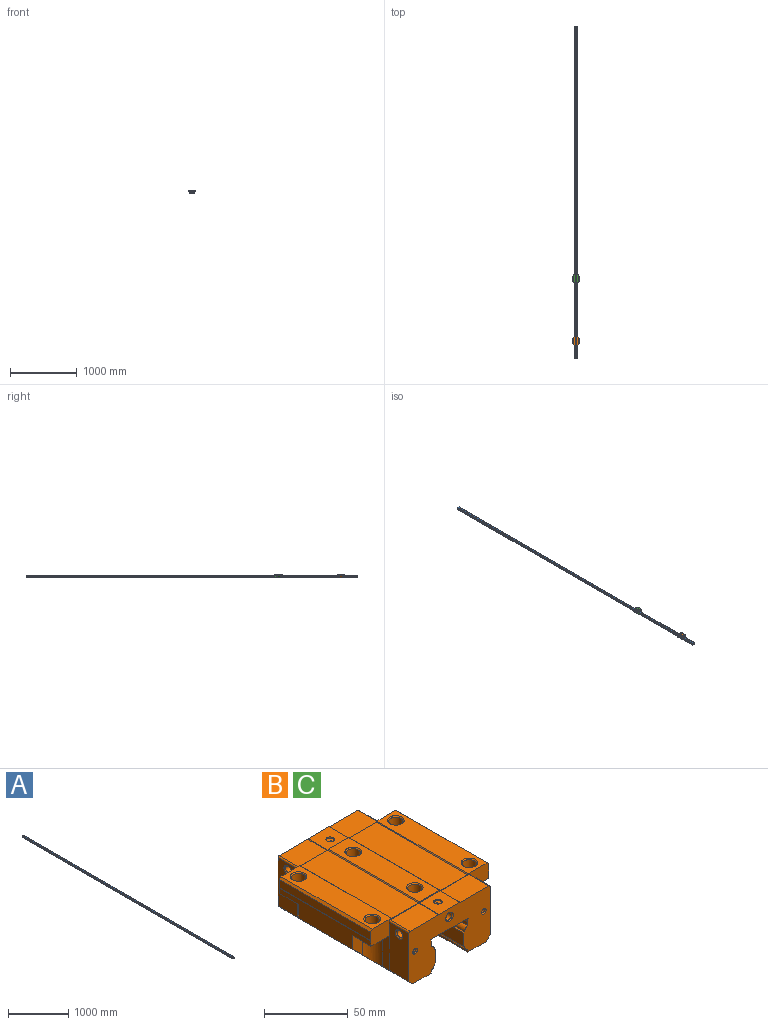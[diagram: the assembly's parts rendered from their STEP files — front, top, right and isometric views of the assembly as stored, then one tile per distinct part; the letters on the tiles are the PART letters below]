
ASSEMBLY  parts=3 mates=4
PART A: 240 faces, bbox 34x4956.5x31.9 mm
  f0: cylinder r=4.5mm len=18.05mm, axis (0,0,1), area 510.3mm2, adj f1,f184
  f1: plane 15x15mm, normal (0,0,1), area 113.1mm2, adj f0,f2
  f2: cylinder r=7.5mm len=15mm, axis (0,0,1), area 636.2mm2, adj f1,f210
  f3: cylinder r=4.5mm len=18.05mm, axis (0,0,1), area 510.3mm2, adj f4,f184
  f4: plane 15x15mm, normal (0,0,1), area 113.1mm2, adj f3,f5
  f5: cylinder r=7.5mm len=15mm, axis (0,0,1), area 636.2mm2, adj f4,f210
  f6: cylinder r=4.5mm len=18.05mm, axis (0,0,1), area 510.3mm2, adj f7,f184
  f7: plane 15x15mm, normal (0,0,1), area 113.1mm2, adj f6,f8
  f8: cylinder r=7.5mm len=15mm, axis (0,0,1), area 636.2mm2, adj f7,f210
  f9: cylinder r=4.5mm len=18.05mm, axis (0,0,1), area 510.3mm2, adj f10,f184
  f10: plane 15x15mm, normal (0,0,1), area 113.1mm2, adj f9,f11
  f11: cylinder r=7.5mm len=15mm, axis (0,0,1), area 636.2mm2, adj f10,f210
  f12: cylinder r=4.5mm len=18.05mm, axis (0,0,1), area 510.3mm2, adj f13,f184
  f13: plane 15x15mm, normal (0,0,1), area 113.1mm2, adj f12,f14
  f14: cylinder r=7.5mm len=15mm, axis (0,0,1), area 636.2mm2, adj f13,f210
  f15: cylinder r=4.5mm len=18.05mm, axis (0,0,1), area 510.3mm2, adj f16,f184
  f16: plane 15x15mm, normal (0,0,1), area 113.1mm2, adj f15,f17
  f17: cylinder r=7.5mm len=15mm, axis (0,0,1), area 636.2mm2, adj f16,f210
  f18: cylinder r=4.5mm len=18.05mm, axis (0,0,1), area 510.3mm2, adj f19,f184
  f19: plane 15x15mm, normal (0,0,1), area 113.1mm2, adj f18,f20
  f20: cylinder r=7.5mm len=15mm, axis (0,0,1), area 636.2mm2, adj f19,f210
  f21: cylinder r=4.5mm len=18.05mm, axis (0,0,1), area 510.3mm2, adj f22,f184
  f22: plane 15x15mm, normal (0,0,1), area 113.1mm2, adj f21,f23
  f23: cylinder r=7.5mm len=15mm, axis (0,0,1), area 636.2mm2, adj f22,f210
  f24: cylinder r=4.5mm len=18.05mm, axis (0,0,1), area 510.3mm2, adj f25,f184
  f25: plane 15x15mm, normal (0,0,1), area 113.1mm2, adj f24,f26
  f26: cylinder r=7.5mm len=15mm, axis (0,0,1), area 636.2mm2, adj f25,f210
  f27: cylinder r=4.5mm len=18.05mm, axis (0,0,1), area 510.3mm2, adj f28,f184
  f28: plane 15x15mm, normal (0,0,1), area 113.1mm2, adj f27,f29
  f29: cylinder r=7.5mm len=15mm, axis (0,0,1), area 636.2mm2, adj f28,f210
  f30: cylinder r=4.5mm len=18.05mm, axis (0,0,1), area 510.3mm2, adj f31,f184
  f31: plane 15x15mm, normal (0,0,1), area 113.1mm2, adj f30,f32
  f32: cylinder r=7.5mm len=15mm, axis (0,0,1), area 636.2mm2, adj f31,f210
  f33: cylinder r=4.5mm len=18.05mm, axis (0,0,1), area 510.3mm2, adj f34,f184
  f34: plane 15x15mm, normal (0,0,1), area 113.1mm2, adj f33,f35
  f35: cylinder r=7.5mm len=15mm, axis (0,0,1), area 636.2mm2, adj f34,f210
  f36: cylinder r=4.5mm len=18.05mm, axis (0,0,1), area 510.3mm2, adj f37,f184
  f37: plane 15x15mm, normal (0,0,1), area 113.1mm2, adj f36,f38
  f38: cylinder r=7.5mm len=15mm, axis (0,0,1), area 636.2mm2, adj f37,f210
  f39: cylinder r=4.5mm len=18.05mm, axis (0,0,1), area 510.3mm2, adj f40,f184
  f40: plane 15x15mm, normal (0,0,1), area 113.1mm2, adj f39,f41
  f41: cylinder r=7.5mm len=15mm, axis (0,0,1), area 636.2mm2, adj f40,f210
  f42: cylinder r=4.5mm len=18.05mm, axis (0,0,1), area 510.3mm2, adj f43,f184
  f43: plane 15x15mm, normal (0,0,1), area 113.1mm2, adj f42,f44
  f44: cylinder r=7.5mm len=15mm, axis (0,0,1), area 636.2mm2, adj f43,f210
  f45: cylinder r=4.5mm len=18.05mm, axis (0,0,1), area 510.3mm2, adj f46,f184
  f46: plane 15x15mm, normal (0,0,1), area 113.1mm2, adj f45,f47
  f47: cylinder r=7.5mm len=15mm, axis (0,0,1), area 636.2mm2, adj f46,f210
  f48: cylinder r=4.5mm len=18.05mm, axis (0,0,1), area 510.3mm2, adj f49,f184
  f49: plane 15x15mm, normal (0,0,1), area 113.1mm2, adj f48,f50
  f50: cylinder r=7.5mm len=15mm, axis (0,0,1), area 636.2mm2, adj f49,f210
  f51: cylinder r=4.5mm len=18.05mm, axis (0,0,1), area 510.3mm2, adj f52,f184
  f52: plane 15x15mm, normal (0,0,1), area 113.1mm2, adj f51,f53
  f53: cylinder r=7.5mm len=15mm, axis (0,0,1), area 636.2mm2, adj f52,f210
  f54: cylinder r=4.5mm len=18.05mm, axis (0,0,1), area 510.3mm2, adj f55,f184
  f55: plane 15x15mm, normal (0,0,1), area 113.1mm2, adj f54,f56
  f56: cylinder r=7.5mm len=15mm, axis (0,0,1), area 636.2mm2, adj f55,f210
  f57: cylinder r=4.5mm len=18.05mm, axis (0,0,1), area 510.3mm2, adj f58,f184
  f58: plane 15x15mm, normal (0,0,1), area 113.1mm2, adj f57,f59
  f59: cylinder r=7.5mm len=15mm, axis (0,0,1), area 636.2mm2, adj f58,f210
  f60: cylinder r=4.5mm len=18.05mm, axis (0,0,1), area 510.3mm2, adj f61,f184
  f61: plane 15x15mm, normal (0,0,1), area 113.1mm2, adj f60,f62
  f62: cylinder r=7.5mm len=15mm, axis (0,0,1), area 636.2mm2, adj f61,f210
  f63: cylinder r=4.5mm len=18.05mm, axis (0,0,1), area 510.3mm2, adj f64,f184
  f64: plane 15x15mm, normal (0,0,1), area 113.1mm2, adj f63,f65
  f65: cylinder r=7.5mm len=15mm, axis (0,0,1), area 636.2mm2, adj f64,f210
  f66: cylinder r=4.5mm len=18.05mm, axis (0,0,1), area 510.3mm2, adj f67,f184
  f67: plane 15x15mm, normal (0,0,1), area 113.1mm2, adj f66,f68
  f68: cylinder r=7.5mm len=15mm, axis (0,0,1), area 636.2mm2, adj f67,f210
  f69: cylinder r=4.5mm len=18.05mm, axis (0,0,1), area 510.3mm2, adj f70,f184
  f70: plane 15x15mm, normal (0,0,1), area 113.1mm2, adj f69,f71
  f71: cylinder r=7.5mm len=15mm, axis (0,0,1), area 636.2mm2, adj f70,f210
  f72: cylinder r=4.5mm len=18.05mm, axis (0,0,1), area 510.3mm2, adj f73,f184
  f73: plane 15x15mm, normal (0,0,1), area 113.1mm2, adj f72,f74
  f74: cylinder r=7.5mm len=15mm, axis (0,0,1), area 636.2mm2, adj f73,f210
  f75: cylinder r=4.5mm len=18.05mm, axis (0,0,1), area 510.3mm2, adj f76,f184
  f76: plane 15x15mm, normal (0,0,1), area 113.1mm2, adj f75,f77
  f77: cylinder r=7.5mm len=15mm, axis (0,0,1), area 636.2mm2, adj f76,f210
  f78: cylinder r=4.5mm len=18.05mm, axis (0,0,1), area 510.3mm2, adj f79,f184
  f79: plane 15x15mm, normal (0,0,1), area 113.1mm2, adj f78,f80
  f80: cylinder r=7.5mm len=15mm, axis (0,0,1), area 636.2mm2, adj f79,f210
  f81: cylinder r=4.5mm len=18.05mm, axis (0,0,1), area 510.3mm2, adj f82,f184
  f82: plane 15x15mm, normal (0,0,1), area 113.1mm2, adj f81,f83
  f83: cylinder r=7.5mm len=15mm, axis (0,0,1), area 636.2mm2, adj f82,f210
  f84: cylinder r=4.5mm len=18.05mm, axis (0,0,1), area 510.3mm2, adj f85,f184
  f85: plane 15x15mm, normal (0,0,1), area 113.1mm2, adj f84,f86
  f86: cylinder r=7.5mm len=15mm, axis (0,0,1), area 636.2mm2, adj f85,f210
  f87: cylinder r=4.5mm len=18.05mm, axis (0,0,1), area 510.3mm2, adj f88,f184
  f88: plane 15x15mm, normal (0,0,1), area 113.1mm2, adj f87,f89
  f89: cylinder r=7.5mm len=15mm, axis (0,0,1), area 636.2mm2, adj f88,f210
  f90: cylinder r=4.5mm len=18.05mm, axis (0,0,1), area 510.3mm2, adj f91,f184
  f91: plane 15x15mm, normal (0,0,1), area 113.1mm2, adj f90,f92
  f92: cylinder r=7.5mm len=15mm, axis (0,0,1), area 636.2mm2, adj f91,f210
  f93: cylinder r=4.5mm len=18.05mm, axis (0,0,1), area 510.3mm2, adj f94,f184
  f94: plane 15x15mm, normal (0,0,1), area 113.1mm2, adj f93,f95
  f95: cylinder r=7.5mm len=15mm, axis (0,0,1), area 636.2mm2, adj f94,f210
  f96: cylinder r=4.5mm len=18.05mm, axis (0,0,1), area 510.3mm2, adj f97,f184
  f97: plane 15x15mm, normal (0,0,1), area 113.1mm2, adj f96,f98
  f98: cylinder r=7.5mm len=15mm, axis (0,0,1), area 636.2mm2, adj f97,f210
  f99: cylinder r=4.5mm len=18.05mm, axis (0,0,1), area 510.3mm2, adj f100,f184
  f100: plane 15x15mm, normal (0,0,1), area 113.1mm2, adj f99,f101
  f101: cylinder r=7.5mm len=15mm, axis (0,0,1), area 636.2mm2, adj f100,f210
  f102: cylinder r=4.5mm len=18.05mm, axis (0,0,1), area 510.3mm2, adj f103,f184
  f103: plane 15x15mm, normal (0,0,1), area 113.1mm2, adj f102,f104
  f104: cylinder r=7.5mm len=15mm, axis (0,0,1), area 636.2mm2, adj f103,f210
  f105: cylinder r=4.5mm len=18.05mm, axis (0,0,1), area 510.3mm2, adj f106,f184
  f106: plane 15x15mm, normal (0,0,1), area 113.1mm2, adj f105,f107
  f107: cylinder r=7.5mm len=15mm, axis (0,0,1), area 636.2mm2, adj f106,f210
  f108: cylinder r=4.5mm len=18.05mm, axis (0,0,1), area 510.3mm2, adj f109,f184
  f109: plane 15x15mm, normal (0,0,1), area 113.1mm2, adj f108,f110
  f110: cylinder r=7.5mm len=15mm, axis (0,0,1), area 636.2mm2, adj f109,f210
  f111: cylinder r=4.5mm len=18.05mm, axis (0,0,1), area 510.3mm2, adj f112,f184
  f112: plane 15x15mm, normal (0,0,1), area 113.1mm2, adj f111,f113
  f113: cylinder r=7.5mm len=15mm, axis (0,0,1), area 636.2mm2, adj f112,f210
  f114: cylinder r=4.5mm len=18.05mm, axis (0,0,1), area 510.3mm2, adj f115,f184
  f115: plane 15x15mm, normal (0,0,1), area 113.1mm2, adj f114,f116
  f116: cylinder r=7.5mm len=15mm, axis (0,0,1), area 636.2mm2, adj f115,f210
  f117: cylinder r=4.5mm len=18.05mm, axis (0,0,1), area 510.3mm2, adj f118,f184
  f118: plane 15x15mm, normal (0,0,1), area 113.1mm2, adj f117,f119
  f119: cylinder r=7.5mm len=15mm, axis (0,0,1), area 636.2mm2, adj f118,f210
  f120: cylinder r=4.5mm len=18.05mm, axis (0,0,1), area 510.3mm2, adj f121,f184
  f121: plane 15x15mm, normal (0,0,1), area 113.1mm2, adj f120,f122
  f122: cylinder r=7.5mm len=15mm, axis (0,0,1), area 636.2mm2, adj f121,f210
  f123: cylinder r=4.5mm len=18.05mm, axis (0,0,1), area 510.3mm2, adj f124,f184
  f124: plane 15x15mm, normal (0,0,1), area 113.1mm2, adj f123,f125
  f125: cylinder r=7.5mm len=15mm, axis (0,0,1), area 636.2mm2, adj f124,f210
  f126: cylinder r=4.5mm len=18.05mm, axis (0,0,1), area 510.3mm2, adj f127,f184
  f127: plane 15x15mm, normal (0,0,1), area 113.1mm2, adj f126,f128
  f128: cylinder r=7.5mm len=15mm, axis (0,0,1), area 636.2mm2, adj f127,f210
  f129: cylinder r=4.5mm len=18.05mm, axis (0,0,1), area 510.3mm2, adj f130,f184
  f130: plane 15x15mm, normal (0,0,1), area 113.1mm2, adj f129,f131
  f131: cylinder r=7.5mm len=15mm, axis (0,0,1), area 636.2mm2, adj f130,f210
  f132: cylinder r=4.5mm len=18.05mm, axis (0,0,1), area 510.3mm2, adj f133,f184
  f133: plane 15x15mm, normal (0,0,1), area 113.1mm2, adj f132,f134
  f134: cylinder r=7.5mm len=15mm, axis (0,0,1), area 636.2mm2, adj f133,f210
  f135: cylinder r=4.5mm len=18.05mm, axis (0,0,1), area 510.3mm2, adj f136,f184
  f136: plane 15x15mm, normal (0,0,1), area 113.1mm2, adj f135,f137
  f137: cylinder r=7.5mm len=15mm, axis (0,0,1), area 636.2mm2, adj f136,f210
  f138: cylinder r=4.5mm len=18.05mm, axis (0,0,1), area 510.3mm2, adj f139,f184
  f139: plane 15x15mm, normal (0,0,1), area 113.1mm2, adj f138,f140
  f140: cylinder r=7.5mm len=15mm, axis (0,0,1), area 636.2mm2, adj f139,f210
  f141: cylinder r=4.5mm len=18.05mm, axis (0,0,1), area 510.3mm2, adj f142,f184
  f142: plane 15x15mm, normal (0,0,1), area 113.1mm2, adj f141,f143
  f143: cylinder r=7.5mm len=15mm, axis (0,0,1), area 636.2mm2, adj f142,f210
  f144: cylinder r=4.5mm len=18.05mm, axis (0,0,1), area 510.3mm2, adj f145,f184
  f145: plane 15x15mm, normal (0,0,1), area 113.1mm2, adj f144,f146
  f146: cylinder r=7.5mm len=15mm, axis (0,0,1), area 636.2mm2, adj f145,f210
  f147: cylinder r=4.5mm len=18.05mm, axis (0,0,1), area 510.3mm2, adj f148,f184
  f148: plane 15x15mm, normal (0,0,1), area 113.1mm2, adj f147,f149
  f149: cylinder r=7.5mm len=15mm, axis (0,0,1), area 636.2mm2, adj f148,f210
  f150: cylinder r=4.5mm len=18.05mm, axis (0,0,1), area 510.3mm2, adj f151,f184
  f151: plane 15x15mm, normal (0,0,1), area 113.1mm2, adj f150,f152
  f152: cylinder r=7.5mm len=15mm, axis (0,0,1), area 636.2mm2, adj f151,f210
  f153: cylinder r=4.5mm len=18.05mm, axis (0,0,1), area 510.3mm2, adj f154,f184
  f154: plane 15x15mm, normal (0,0,1), area 113.1mm2, adj f153,f155
  f155: cylinder r=7.5mm len=15mm, axis (0,0,1), area 636.2mm2, adj f154,f210
  f156: cylinder r=4.5mm len=18.05mm, axis (0,0,1), area 510.3mm2, adj f157,f184
  f157: plane 15x15mm, normal (0,0,1), area 113.1mm2, adj f156,f158
  f158: cylinder r=7.5mm len=15mm, axis (0,0,1), area 636.2mm2, adj f157,f210
  f159: cylinder r=4.5mm len=18.05mm, axis (0,0,1), area 510.3mm2, adj f160,f184
  f160: plane 15x15mm, normal (0,0,1), area 113.1mm2, adj f159,f161
  f161: cylinder r=7.5mm len=15mm, axis (0,0,1), area 636.2mm2, adj f160,f210
  f162: cylinder r=4.5mm len=18.05mm, axis (0,0,1), area 510.3mm2, adj f163,f184
  f163: plane 15x15mm, normal (0,0,1), area 113.1mm2, adj f162,f164
  f164: cylinder r=7.5mm len=15mm, axis (0,0,1), area 636.2mm2, adj f163,f210
  f165: cylinder r=4.5mm len=18.05mm, axis (0,0,1), area 510.3mm2, adj f166,f184
  f166: plane 15x15mm, normal (0,0,1), area 113.1mm2, adj f165,f167
  f167: cylinder r=7.5mm len=15mm, axis (0,0,1), area 636.2mm2, adj f166,f210
  f168: cylinder r=4.5mm len=18.05mm, axis (0,0,1), area 510.3mm2, adj f169,f184
  f169: plane 15x15mm, normal (0,0,1), area 113.1mm2, adj f168,f170
  f170: cylinder r=7.5mm len=15mm, axis (0,0,1), area 636.2mm2, adj f169,f210
  f171: cylinder r=4.5mm len=18.05mm, axis (0,0,1), area 510.3mm2, adj f172,f184
  f172: plane 15x15mm, normal (0,0,1), area 113.1mm2, adj f171,f173
  f173: cylinder r=7.5mm len=15mm, axis (0,0,1), area 636.2mm2, adj f172,f210
  f174: cylinder r=4.5mm len=18.05mm, axis (0,0,1), area 510.3mm2, adj f175,f184
  f175: plane 15x15mm, normal (0,0,1), area 113.1mm2, adj f174,f176
  f176: cylinder r=7.5mm len=15mm, axis (0,0,1), area 636.2mm2, adj f175,f210
  f177: cylinder r=4.5mm len=18.05mm, axis (0,0,1), area 510.3mm2, adj f178,f184
  f178: plane 15x15mm, normal (0,0,1), area 113.1mm2, adj f177,f179
  f179: cylinder r=7.5mm len=15mm, axis (0,0,1), area 636.2mm2, adj f178,f210
  f180: plane 4956.54x5.07mm, normal (-1,0,0), area 25140mm2, adj f181,f231,f232,f233
  f181: plane 4956.54x1mm, normal (-0.71,0,-0.71), area 7009.6mm2, adj f180,f182,f232,f233
  f182: plane 4956.54x9.8mm, normal (0,0,-1), area 48574.1mm2, adj f181,f183,f232,f233
  f183: plane 4956.54x0.3mm, normal (0.71,0,-0.71), area 2102.9mm2, adj f182,f184,f232,f233
  f184: plane 4956.54x11.8mm, normal (0,0,-1), area 54543.4mm2, adj f0,f3,f6,f9,f12,f15,f18,f21
  f185: plane 4956.54x0.3mm, normal (-0.71,0,-0.71), area 2102.9mm2, adj f184,f186,f232,f233
  f186: plane 4956.54x9.8mm, normal (0,0,-1), area 48574.1mm2, adj f185,f187,f232,f233
  f187: plane 4956.54x1mm, normal (0.71,0,-0.71), area 7009.6mm2, adj f186,f188,f232,f233
  f188: plane 4956.54x5.07mm, normal (1,0,0), area 25140mm2, adj f187,f189,f232,f233
  f189: cylinder r=0.8mm len=4956.54mm, axis (0,1,0), area 4152.3mm2, adj f188,f190,f232,f233
  f190: plane 4956.54x0.7mm, normal (0.5,0,0.87), area 4006.3mm2, adj f189,f191,f232,f233
  f191: cylinder r=0.8mm len=4956.54mm, axis (0,1,0), area 4152.4mm2, adj f190,f192,f232,f233
  f192: plane 4956.54x1.75mm, normal (1,0,0), area 8650.2mm2, adj f191,f193,f232,f233
  f193: cylinder r=0.3mm len=4956.54mm, axis (0,1,0), area 1979.4mm2, adj f192,f194,f232,f233
  f194: cylinder r=3.24mm len=4956.54mm, axis (0,1,0), area 18238.7mm2, adj f193,f195,f232,f233
  f195: cylinder r=0.3mm len=4956.54mm, axis (0,1,0), area 877.1mm2, adj f194,f196,f232,f233
  f196: plane 4956.54x0.8mm, normal (0.71,0,0.71), area 5574.5mm2, adj f195,f197,f232,f233
  f197: cylinder r=0.8mm len=4956.54mm, axis (0,1,0), area 3114.3mm2, adj f196,f198,f232,f233
  f198: plane 4956.54x9.14mm, normal (1,0,0), area 45289.2mm2, adj f197,f199,f232,f233
  f199: cylinder r=0.8mm len=4956.54mm, axis (0,1,0), area 3114.3mm2, adj f198,f200,f232,f233
  f200: plane 4956.54x0.8mm, normal (0.71,0,-0.71), area 5574.5mm2, adj f199,f201,f232,f233
  f201: cylinder r=0.3mm len=4956.54mm, axis (0,1,0), area 877.1mm2, adj f200,f202,f232,f233
  f202: cylinder r=3.24mm len=4956.54mm, axis (0,1,0), area 18238.7mm2, adj f201,f203,f232,f233
  f203: cylinder r=0.3mm len=4956.54mm, axis (0,1,0), area 1979.4mm2, adj f202,f204,f232,f233
  f204: plane 4956.54x1.96mm, normal (1,0,0), area 9714.9mm2, adj f203,f205,f232,f233
  f205: cylinder r=0.5mm len=4956.54mm, axis (0,1,0), area 1946.3mm2, adj f204,f206,f232,f233
  f206: plane 4956.54x0.3mm, normal (0.71,0,0.71), area 2099mm2, adj f205,f207,f232,f233
  f207: cylinder r=0.5mm len=4956.54mm, axis (0,1,0), area 2595.3mm2, adj f206,f208,f232,f233
  f208: plane 4956.54x0.73mm, normal (0.97,0,-0.26), area 3754.9mm2, adj f207,f209,f232,f233
  f209: cylinder r=0.5mm len=4956.54mm, axis (0,1,0), area 4541.6mm2, adj f208,f210,f232,f233
  f210: plane 4956.54x29.28mm, normal (0,0,1), area 134147.6mm2, adj f2,f5,f8,f11,f14,f17,f20,f23
  f211: cylinder r=0.5mm len=4956.54mm, axis (0,1,0), area 4541.6mm2, adj f210,f212,f232,f233
  f212: plane 4956.54x0.73mm, normal (-0.97,0,-0.26), area 3754.9mm2, adj f211,f213,f232,f233
  f213: cylinder r=0.5mm len=4956.54mm, axis (0,1,0), area 2595.3mm2, adj f212,f214,f232,f233
  f214: plane 4956.54x0.3mm, normal (-0.71,0,0.71), area 2099mm2, adj f213,f215,f232,f233
  f215: cylinder r=0.5mm len=4956.54mm, axis (0,1,0), area 1946.3mm2, adj f214,f216,f232,f233
  f216: plane 4956.54x1.96mm, normal (-1,0,0), area 9714.9mm2, adj f215,f217,f232,f233
  f217: cylinder r=0.3mm len=4956.54mm, axis (0,1,0), area 1979.4mm2, adj f216,f218,f232,f233
  f218: cylinder r=3.24mm len=4956.54mm, axis (0,1,0), area 18238.7mm2, adj f217,f219,f232,f233
  f219: cylinder r=0.3mm len=4956.54mm, axis (0,1,0), area 877.1mm2, adj f218,f220,f232,f233
  f220: plane 4956.54x0.8mm, normal (-0.71,0,-0.71), area 5574.5mm2, adj f219,f221,f232,f233
  f221: cylinder r=0.8mm len=4956.54mm, axis (0,1,0), area 3114.3mm2, adj f220,f222,f232,f233
  f222: plane 4956.54x9.14mm, normal (-1,0,0), area 45289.2mm2, adj f221,f223,f232,f233
  f223: cylinder r=0.8mm len=4956.54mm, axis (0,1,0), area 3114.3mm2, adj f222,f224,f232,f233
  f224: plane 4956.54x0.8mm, normal (-0.71,0,0.71), area 5574.5mm2, adj f223,f225,f232,f233
  f225: cylinder r=0.3mm len=4956.54mm, axis (0,1,0), area 877.1mm2, adj f224,f226,f232,f233
  f226: cylinder r=3.24mm len=4956.54mm, axis (0,1,0), area 18238.7mm2, adj f225,f227,f232,f233
  f227: cylinder r=0.3mm len=4956.54mm, axis (0,1,0), area 1979.4mm2, adj f226,f228,f232,f233
  f228: plane 4956.54x1.75mm, normal (-1,0,0), area 8650.2mm2, adj f227,f229,f232,f233
  f229: cylinder r=0.8mm len=4956.54mm, axis (0,1,0), area 4152.4mm2, adj f228,f230,f232,f233
  f230: plane 4956.54x0.7mm, normal (-0.5,0,0.87), area 4006.3mm2, adj f229,f231,f232,f233
  f231: cylinder r=0.8mm len=4956.54mm, axis (0,1,0), area 4152.3mm2, adj f180,f230,f232,f233
  f232: plane 34x31.85mm, normal (0,-1,0), area 893.9mm2, adj f180,f181,f182,f183,f184,f185,f186,f187
  f233: plane 34x31.85mm, normal (0,1,0), area 893.9mm2, adj f180,f181,f182,f183,f184,f185,f186,f187
  f234: cylinder r=4.5mm len=18.05mm, axis (0,0,1), area 510.3mm2, adj f184,f235
  f235: plane 15x15mm, normal (0,0,1), area 113.1mm2, adj f234,f236
  f236: cylinder r=7.5mm len=15mm, axis (0,0,1), area 636.2mm2, adj f210,f235
  f237: cylinder r=4.5mm len=18.05mm, axis (0,0,1), area 510.3mm2, adj f184,f238
  f238: plane 15x15mm, normal (0,0,1), area 113.1mm2, adj f237,f239
  f239: cylinder r=7.5mm len=15mm, axis (0,0,1), area 636.2mm2, adj f210,f238
PART B: 150 faces, bbox 100x110.5x40.4 mm
  f0: plane 0.8x0.8mm, normal (0,0,1), area 0.5mm2, adj f5
  f1: cone r=1.25mm half-angle=59deg, axis (0,-1,0), area 5.7mm2, adj f8
  f2: cone r=2.5mm half-angle=59deg, axis (0,-1,0), area 22.9mm2, adj f9
  f3: cone r=1.25mm half-angle=59deg, axis (0,-1,0), area 5.7mm2, adj f10
  f4: cone r=2.5mm half-angle=59deg, axis (-1,0,0), area 22.9mm2, adj f11
  f5: cylinder r=0.4mm len=6.5mm, axis (0,0,1), area 16.3mm2, adj f0,f12
  f6: cone r=2.5mm half-angle=59deg, axis (1,0,0), area 22.9mm2, adj f13
  f7: plane 0.8x0.8mm, normal (0,0,1), area 0.5mm2, adj f14
  f8: cylinder r=1.25mm len=5.8mm, axis (0,1,0), area 45.6mm2, adj f1,f21
  f9: cylinder r=2.5mm len=7.3mm, axis (0,1,0), area 114.7mm2, adj f2,f22
  f10: cylinder r=1.25mm len=5.8mm, axis (0,1,0), area 45.6mm2, adj f3,f23
  f11: cylinder r=2.5mm len=7.3mm, axis (1,0,0), area 114.7mm2, adj f4,f24
  f12: plane 5x5mm, normal (0,0,1), area 19.1mm2, adj f5,f26
  f13: cylinder r=2.5mm len=7.3mm, axis (1,0,0), area 114.7mm2, adj f6,f27
  f14: cylinder r=0.4mm len=6.5mm, axis (0,0,1), area 16.3mm2, adj f7,f28
  f15: cone r=2.5mm half-angle=59deg, axis (-1,0,0), area 22.9mm2, adj f38
  f16: cone r=1.25mm half-angle=59deg, axis (0,1,0), area 5.7mm2, adj f40
  f17: cone r=1.25mm half-angle=59deg, axis (0,1,0), area 5.7mm2, adj f41
  f18: cone r=2.5mm half-angle=59deg, axis (0,1,0), area 22.9mm2, adj f42
  f19: plane 17x17mm, normal (0,0,-1), area 170.2mm2, adj f31,f43
  f20: plane 17x17mm, normal (0,0,-1), area 170.2mm2, adj f30,f44
  f21: cone r=1.25mm half-angle=45deg, axis (0,-1,0), area 10mm2, adj f8,f49
  f22: cone r=2.5mm half-angle=45deg, axis (0,-1,0), area 17.7mm2, adj f9,f49
  f23: cone r=1.25mm half-angle=45deg, axis (0,-1,0), area 10mm2, adj f10,f49
  f24: cone r=2.5mm half-angle=45deg, axis (-1,0,0), area 17.7mm2, adj f11,f54
  f25: plane 16.75x3.22mm, normal (-0.71,0,-0.71), area 76.3mm2, adj f34,f45,f47,f49,f54
  f26: cylinder r=2.5mm len=5mm, axis (0,0,1), area 15.7mm2, adj f12,f58
  f27: cone r=2.5mm half-angle=45deg, axis (1,0,0), area 17.7mm2, adj f13,f62
  f28: plane 5x5mm, normal (0,0,1), area 19.1mm2, adj f14,f63
  f29: cylinder r=4.25mm len=10.6mm, axis (0,0,1), area 283.1mm2, adj f52,f64
  f30: cylinder r=4.25mm len=9.5mm, axis (0,0,-1), area 253.7mm2, adj f20,f66
  f31: cylinder r=4.25mm len=9.5mm, axis (0,0,-1), area 253.7mm2, adj f19,f67
  f32: cylinder r=4.25mm len=10.6mm, axis (0,0,1), area 283.1mm2, adj f33,f68
  f33: cone r=4.25mm half-angle=45deg, axis (0,0,-1), area 28.6mm2, adj f32,f70
  f34: plane 26.83x1.7mm, normal (0,1,0), area 44.2mm2, adj f25,f36,f54,f70
  f35: cylinder r=8.5mm len=26.9mm, axis (0,0,1), area 317.9mm2, adj f36,f70,f71,f72
  f36: plane 26.9x7.5mm, normal (-1,0,0), area 201.7mm2, adj f34,f35,f47,f70,f72
  f37: cylinder r=4.25mm len=10.6mm, axis (0,0,1), area 283.1mm2, adj f69,f73
  f38: cylinder r=2.5mm len=7.3mm, axis (1,0,0), area 114.7mm2, adj f15,f77
  f39: cone r=2.5mm half-angle=59deg, axis (1,0,0), area 22.9mm2, adj f79
  f40: cylinder r=1.25mm len=5.8mm, axis (0,1,0), area 45.6mm2, adj f16,f80
  f41: cylinder r=1.25mm len=5.8mm, axis (0,1,0), area 45.6mm2, adj f17,f81
  f42: cylinder r=2.5mm len=7.3mm, axis (0,1,0), area 114.7mm2, adj f18,f82
  f43: cylinder r=8.5mm len=17mm, axis (0,0,-1), area 288.4mm2, adj f19,f91
  f44: cylinder r=8.5mm len=17mm, axis (0,0,-1), area 288.4mm2, adj f20,f91
  f45: plane 16.75x15.48mm, normal (0,0,-1), area 259.3mm2, adj f25,f47,f49,f100
  f46: plane 77x15.5mm, normal (0,0,-1), area 1193.5mm2, adj f47,f48,f72,f100
  f47: plane 17x1.57mm, normal (0,-1,0), area 0.9mm2, adj f25,f36,f45,f46,f72,f100
  f48: plane 17x1.57mm, normal (0,1,0), area 0.9mm2, adj f46,f72,f74,f100,f101,f102
  f49: plane 68.4x39.75mm, normal (0,-1,0), area 1979.4mm2, adj f21,f22,f23,f25,f45,f50,f51,f54
  f50: plane 16.75x3.22mm, normal (0.71,0,-0.71), area 76.3mm2, adj f49,f51,f53,f62,f105
  f51: plane 16.75x15.48mm, normal (0,0,-1), area 259.3mm2, adj f49,f50,f103,f105
  f52: cone r=4.95mm half-angle=45deg, axis (0,0,-1), area 28.6mm2, adj f29,f110
  f53: plane 26.83x1.7mm, normal (0,1,0), area 44.2mm2, adj f50,f62,f106,f110
  f54: plane 35.28x16.75mm, normal (-1,0,0), area 558.8mm2, adj f24,f25,f34,f49,f55,f111
  f55: cylinder r=1mm len=16.75mm, axis (0,-1,0), area 26.3mm2, adj f49,f54,f56,f111
  f56: plane 24.15x16.75mm, normal (0,0,1), area 404.5mm2, adj f49,f55,f57,f111
  f57: plane 16.75x0.25mm, normal (-0.71,0,0.71), area 5.9mm2, adj f49,f56,f58,f111
  f58: plane 17.6x16.75mm, normal (0,0,1), area 275.2mm2, adj f26,f49,f57,f59,f111
  f59: plane 16.75x0.25mm, normal (0.71,0,0.71), area 5.9mm2, adj f49,f58,f60,f111
  f60: plane 24.15x16.75mm, normal (0,0,1), area 404.5mm2, adj f49,f59,f61,f111
  f61: cylinder r=1mm len=16.75mm, axis (0,-1,0), area 26.3mm2, adj f49,f60,f62,f111
  f62: plane 35.28x16.75mm, normal (1,0,0), area 558.8mm2, adj f27,f49,f50,f53,f61,f111
  f63: cylinder r=2.5mm len=5mm, axis (0,0,1), area 15.7mm2, adj f28,f115
  f64: cone r=4.25mm half-angle=45deg, axis (0,0,1), area 28.6mm2, adj f29,f119
  f65: cone r=4.25mm half-angle=45deg, axis (0,0,1), area 28.6mm2, adj f108,f119
  f66: cone r=4.95mm half-angle=45deg, axis (0,0,1), area 28.6mm2, adj f30,f123
  f67: cone r=4.95mm half-angle=45deg, axis (0,0,1), area 28.6mm2, adj f31,f123
  f68: cone r=4.25mm half-angle=45deg, axis (0,0,1), area 28.6mm2, adj f32,f127
  f69: cone r=4.25mm half-angle=45deg, axis (0,0,1), area 28.6mm2, adj f37,f127
  f70: plane 17x16mm, normal (0,0,-1), area 179.5mm2, adj f33,f34,f35,f36,f71,f111,f131
  f71: plane 18.4x8.5mm, normal (0,-1,0), area 120.3mm2, adj f35,f70,f72,f131
  f72: plane 77x18.5mm, normal (-0.71,0,-0.71), area 1289.1mm2, adj f35,f36,f46,f47,f48,f71,f74,f75
  f73: cone r=4.95mm half-angle=45deg, axis (0,0,-1), area 28.6mm2, adj f37,f132
  f74: plane 26.9x7.5mm, normal (-1,0,0), area 201.7mm2, adj f48,f72,f75,f78,f132
  f75: cylinder r=8.5mm len=26.9mm, axis (0,0,1), area 317.9mm2, adj f72,f74,f76,f132
  f76: plane 18.4x8.5mm, normal (0,1,0), area 120.3mm2, adj f72,f75,f131,f132
  f77: cone r=3.2mm half-angle=45deg, axis (-1,0,0), area 17.7mm2, adj f38,f133
  f78: plane 26.83x1.7mm, normal (0,-1,0), area 44.2mm2, adj f74,f102,f132,f133
  f79: cylinder r=2.5mm len=7.3mm, axis (1,0,0), area 114.7mm2, adj f39,f134
  f80: cone r=1.95mm half-angle=45deg, axis (0,1,0), area 10mm2, adj f40,f136
  f81: cone r=1.95mm half-angle=45deg, axis (0,1,0), area 10mm2, adj f41,f136
  f82: cone r=3.2mm half-angle=45deg, axis (0,1,0), area 17.7mm2, adj f42,f136
  f83: cylinder r=3.24mm len=110.5mm, axis (0,-1,0), area 495.6mm2, adj f49,f84,f103,f136
  f84: plane 110.5x1.06mm, normal (-0.5,0,-0.87), area 134.8mm2, adj f49,f83,f85,f136
  f85: plane 110.5x9.8mm, normal (-1,0,0), area 1082.9mm2, adj f49,f84,f86,f136
  f86: plane 110.5x1.06mm, normal (-0.5,0,0.87), area 134.8mm2, adj f49,f85,f87,f136
  f87: cylinder r=3.24mm len=110.5mm, axis (0,-1,0), area 495.6mm2, adj f49,f86,f88,f136
  f88: plane 110.5x2.41mm, normal (-1,0,0), area 266.6mm2, adj f49,f87,f89,f136
  f89: plane 110.5x0.41mm, normal (-0.71,0,-0.71), area 63.3mm2, adj f49,f88,f90,f136
  f90: plane 110.5x2.49mm, normal (-0.97,0,0.26), area 284.3mm2, adj f49,f89,f91,f136
  f91: plane 110.5x31.52mm, normal (0,0,-1), area 3029.2mm2, adj f43,f44,f49,f90,f92,f136
  f92: plane 110.5x2.49mm, normal (0.97,0,0.26), area 284.3mm2, adj f49,f91,f93,f136
  f93: plane 110.5x0.41mm, normal (0.71,0,-0.71), area 63.3mm2, adj f49,f92,f94,f136
  f94: plane 110.5x2.41mm, normal (1,0,0), area 266.6mm2, adj f49,f93,f95,f136
  f95: cylinder r=3.24mm len=110.5mm, axis (0,-1,0), area 495.6mm2, adj f49,f94,f96,f136
  f96: plane 110.5x1.06mm, normal (0.5,0,0.87), area 134.8mm2, adj f49,f95,f97,f136
  f97: plane 110.5x9.8mm, normal (1,0,0), area 1082.9mm2, adj f49,f96,f98,f136
  f98: plane 110.5x1.06mm, normal (0.5,0,-0.87), area 134.8mm2, adj f49,f97,f99,f136
  f99: cylinder r=3.24mm len=110.5mm, axis (0,-1,0), area 495.6mm2, adj f49,f98,f100,f136
  f100: plane 110.5x2.2mm, normal (1,0,0), area 241.7mm2, adj f45,f46,f47,f48,f49,f99,f101,f136
  f101: plane 16.75x15.48mm, normal (0,0,-1), area 259.3mm2, adj f48,f100,f102,f136
  f102: plane 16.75x3.22mm, normal (-0.71,0,-0.71), area 76.3mm2, adj f48,f78,f101,f133,f136
  f103: plane 110.5x2.2mm, normal (-1,0,0), area 241.7mm2, adj f49,f51,f83,f104,f105,f136,f137,f138
  f104: plane 77x15.5mm, normal (0,0,-1), area 1193.5mm2, adj f103,f105,f138,f139
  f105: plane 17x1.57mm, normal (0,-1,0), area 0.9mm2, adj f50,f51,f103,f104,f106,f139
  f106: plane 26.9x7.5mm, normal (1,0,0), area 201.7mm2, adj f53,f105,f107,f110,f139
  f107: cylinder r=8.5mm len=26.9mm, axis (0,0,1), area 317.9mm2, adj f106,f109,f110,f139
  f108: cylinder r=4.25mm len=10.6mm, axis (0,0,1), area 283.1mm2, adj f65,f140
  f109: plane 18.4x9mm, normal (0,-1,0), area 125.1mm2, adj f107,f110,f139,f142
  f110: plane 17.5x16mm, normal (0,0,-1), area 187.5mm2, adj f52,f53,f106,f107,f109,f111,f142
  f111: plane 100x12mm, normal (0,-1,0), area 405.4mm2, adj f54,f55,f56,f57,f58,f59,f60,f61
  f112: cylinder r=1mm len=16.75mm, axis (0,-1,0), area 26.3mm2, adj f113,f133,f136,f143
  f113: plane 24.15x16.75mm, normal (0,0,1), area 404.5mm2, adj f112,f114,f136,f143
  f114: plane 16.75x0.25mm, normal (-0.71,0,0.71), area 5.9mm2, adj f113,f115,f136,f143
  f115: plane 17.6x16.75mm, normal (0,0,1), area 275.2mm2, adj f63,f114,f116,f136,f143
  f116: plane 16.75x0.25mm, normal (0.71,0,0.71), area 5.9mm2, adj f115,f117,f136,f143
  f117: plane 24.15x16.75mm, normal (0,0,1), area 404.5mm2, adj f116,f135,f136,f143
  f118: plane 77x1.5mm, normal (0.71,0,0.71), area 163.3mm2, adj f111,f119,f142,f143
  f119: plane 77x16mm, normal (0,0,1), area 1078mm2, adj f64,f65,f111,f118,f120,f143
  f120: plane 77x0.5mm, normal (-0.71,0,0.71), area 54.4mm2, adj f111,f119,f121,f143
  f121: plane 77x23mm, normal (0,0,1), area 1771mm2, adj f111,f120,f122,f143
  f122: plane 77x0.5mm, normal (0.71,0,0.71), area 54.4mm2, adj f111,f121,f123,f143
  f123: plane 77x17mm, normal (0,0,1), area 1155mm2, adj f66,f67,f111,f122,f124,f143
  f124: plane 77x0.5mm, normal (-0.71,0,0.71), area 54.4mm2, adj f111,f123,f125,f143
  f125: plane 77x23mm, normal (0,0,1), area 1771mm2, adj f111,f124,f126,f143
  f126: plane 77x0.5mm, normal (0.71,0,0.71), area 54.4mm2, adj f111,f125,f127,f143
  f127: plane 77x16mm, normal (0,0,1), area 1078mm2, adj f68,f69,f111,f126,f128,f143
  f128: plane 77x1.5mm, normal (-0.71,0,0.71), area 163.3mm2, adj f111,f127,f129,f143
  f129: plane 77x6mm, normal (-1,0,0), area 462mm2, adj f111,f128,f130,f143
  f130: plane 77x0.5mm, normal (-0.71,0,-0.71), area 54.4mm2, adj f111,f129,f131,f143
  f131: plane 77x13.9mm, normal (-1,0,0), area 753.5mm2, adj f70,f71,f72,f76,f111,f130,f132,f143
  f132: plane 17x16mm, normal (0,0,-1), area 179.5mm2, adj f73,f74,f75,f76,f78,f131,f143
  f133: plane 35.28x16.75mm, normal (-1,0,0), area 558.8mm2, adj f77,f78,f102,f112,f136,f143
  f134: cone r=3.2mm half-angle=45deg, axis (1,0,0), area 17.7mm2, adj f79,f145
  f135: cylinder r=1mm len=16.75mm, axis (0,-1,0), area 26.3mm2, adj f117,f136,f143,f145
  f136: plane 68.4x39.75mm, normal (0,1,0), area 1979.4mm2, adj f80,f81,f82,f83,f84,f85,f86,f87
  f137: plane 16.75x15.48mm, normal (0,0,-1), area 259.3mm2, adj f103,f136,f138,f146
  f138: plane 17x1.57mm, normal (0,1,0), area 0.9mm2, adj f103,f104,f137,f139,f146,f147
  f139: plane 77x19mm, normal (0.71,0,-0.71), area 1320.9mm2, adj f104,f105,f106,f107,f109,f138,f141,f142
  f140: cone r=4.25mm half-angle=45deg, axis (0,0,-1), area 28.6mm2, adj f108,f148
  f141: plane 18.4x9mm, normal (0,1,0), area 125.1mm2, adj f139,f142,f144,f148
  f142: plane 77x19.9mm, normal (1,0,0), area 1231.5mm2, adj f109,f110,f111,f118,f139,f141,f143,f148
  f143: plane 100x12mm, normal (0,1,0), area 405.4mm2, adj f112,f113,f114,f115,f116,f117,f118,f119
  f144: cylinder r=8.5mm len=26.9mm, axis (0,0,1), area 317.9mm2, adj f139,f141,f147,f148
  f145: plane 35.28x16.75mm, normal (1,0,0), area 558.8mm2, adj f134,f135,f136,f143,f146,f149
  f146: plane 16.75x3.22mm, normal (0.71,0,-0.71), area 76.3mm2, adj f136,f137,f138,f145,f149
  f147: plane 26.9x7.5mm, normal (1,0,0), area 201.7mm2, adj f138,f139,f144,f148,f149
  f148: plane 17.5x16mm, normal (0,0,-1), area 187.5mm2, adj f140,f141,f142,f143,f144,f147,f149
  f149: plane 26.83x1.7mm, normal (0,-1,0), area 44.2mm2, adj f145,f146,f147,f148
PART C: same geometry as B
PLACE A t=(0.15,-0.43,-0.79)mm
PLACE B t=(0.15,-2225.05,10.54)mm
PLACE C t=(0.15,-1293.51,10.54)mm
MATE planar A.f222 <-> B.f97  axis (-1,0,0) through (-11.6,-0.43,1.79)mm
MATE fastened B.f2 <-> C.f2  axis (0,-1,0) through (0.15,-2280.3,23.84)mm
MATE planar B.f91 <-> A.f210  axis (0,0,-1) through (0.15,-2225.05,15.14)mm
MATE planar C.f97 <-> A.f222  axis (1,0,0) through (-11.6,-1293.51,1.19)mm
